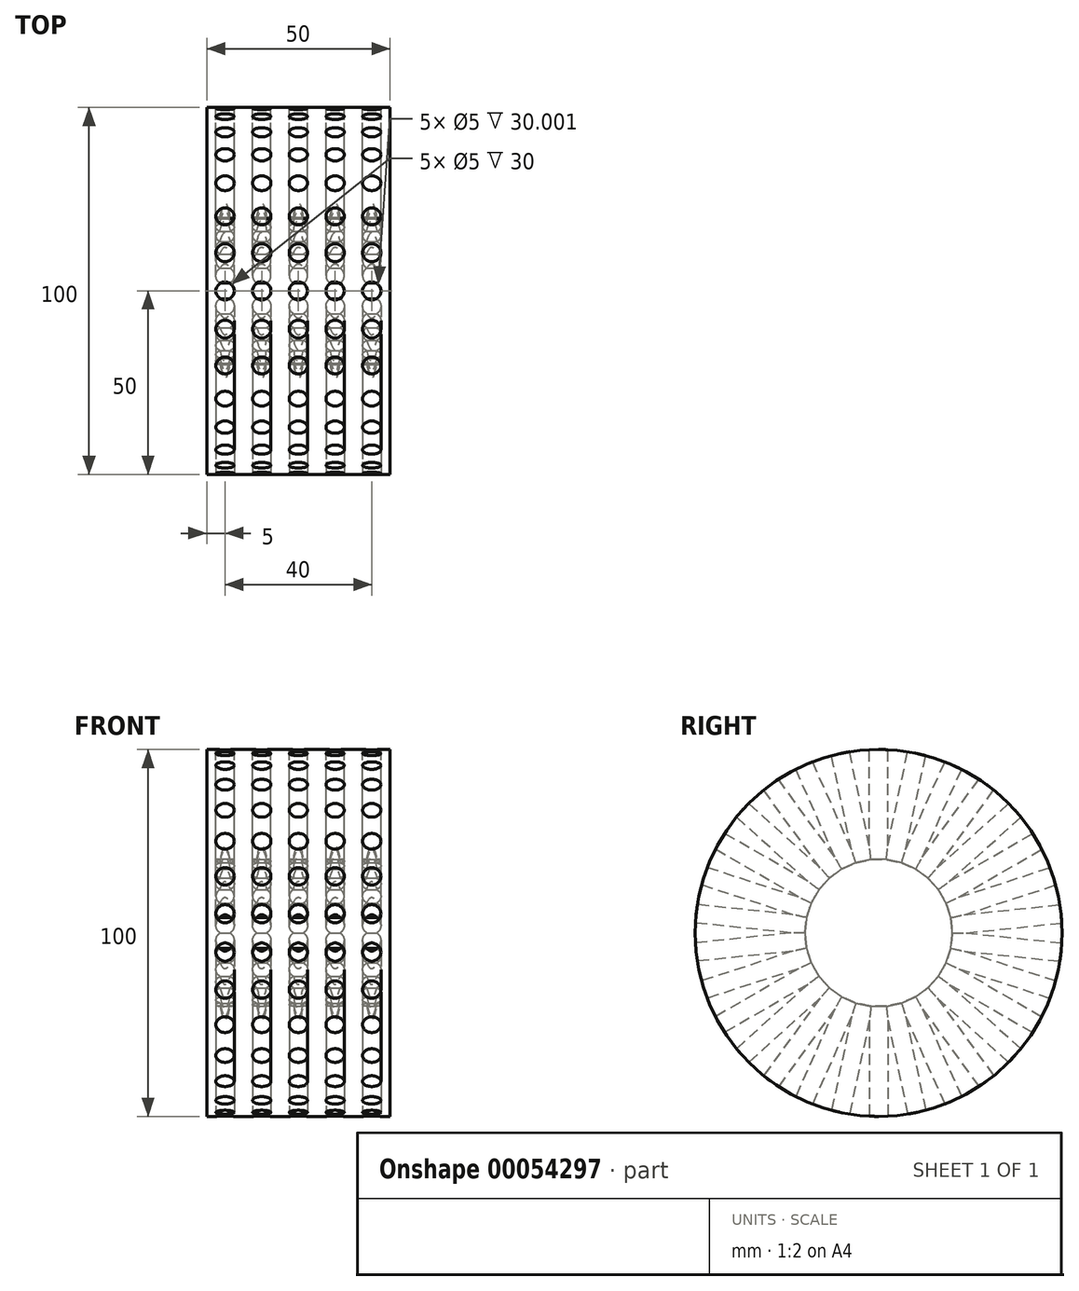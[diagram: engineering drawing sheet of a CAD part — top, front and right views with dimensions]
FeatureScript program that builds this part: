
annotation { "Feature Type Name" : "Feature", "Feature Type Description" : "" }
export const myFeature = defineFeature(function(context is Context, id is Id, definition is map)
    precondition{}
    {
        {
            var Q0;
            Q0=qCreatedBy(makeId("Right.planeOp"),FACE);
            var sketch = newSketch(context, id + "F0", { "sketchPlane" : qUnion([Q0])});
            skCircle(sketch, "E0", {"center": v(0, 0) * mm, "radius": 50 * mm});
            skPoint(sketch, "E1", {"position": v(0, 50) * mm});
            skLineSegment(sketch, "E2", {"start": v(0, 50) * mm, "end": v(0, -50) * mm, "construction": true});
            skSolve(sketch);
        }
        {
            var Q0;
            Q0=makeQuery(id+"F0.imprint","IMPRINT",FACE,{"disambiguationData":[TD([[makeQuery(id+"F0.imprint","IMPRINT",EDGE,{"derivedFrom":sQuery(id+"F0.wireOp",EDGE,"E0")}),1.0]])]});
            extrude(context, id + "F1", {"entities" : qUnion([Q0]), "depth" : 50 * mm});
        }
        {
            var Q0;
            Q0=sQuery(id+"F0.wireOp",VERTEX,"E1");
            var Q1;
            Q1=sQuery(id+"F0.wireOp",EDGE,"E2");
            cPlane(context, id + "F2", {"entities" : qUnion([Q0, Q1]), "cplaneType" : CPlaneType.LINE_POINT, "offset" : 150 * mm, "width" : 150 * mm, "height" : 150 * mm});
        }
        {
            var Q0;
            Q0=qCreatedBy(id+"F2.planeOp",FACE);
            var sketch = newSketch(context, id + "F3", { "sketchPlane" : qUnion([Q0])});
            skLineSegment(sketch, "E3", {"start": v(0, 0) * mm, "end": v(50, 0) * mm, "construction": true});
            skLineSegment(sketch, "E4.0", {"start": v(50, 50) * mm, "end": v(50, -50) * mm, "construction": true});
            skCircle(sketch, "E5", {"center": v(5, 0) * mm, "radius": 2.5 * mm});
            skCircle(sketch, "E6.1.0.0", {"center": v(15, 0) * mm, "radius": 2.5 * mm});
            skCircle(sketch, "E6.2.0.0", {"center": v(25, 0) * mm, "radius": 2.5 * mm});
            skCircle(sketch, "E6.3.0.0", {"center": v(35, 0) * mm, "radius": 2.5 * mm});
            skCircle(sketch, "E6.4.0.0", {"center": v(45, 0) * mm, "radius": 2.5 * mm});
            skLineSegment(sketch, "E6.direction1", {"start": v(5, 0) * mm, "end": v(15, 0) * mm, "construction": true});
            skSolve(sketch);
        }
        {
            var Q0;
            Q0 = qSketchRegion(id + "F3", true);
            extrude(context, id + "F4", {"entities" : qUnion([Q0]), "depth" : 30 * mm});
        }
        {
            var Q0;
            Q0=qCreatedBy(makeId("Front.planeOp"),FACE);
            var sketch = newSketch(context, id + "F5", { "sketchPlane" : qUnion([Q0])});
            skLineSegment(sketch, "E7", {"start": v(0, 0) * mm, "end": v(40.86, 0) * mm, "construction": true});
            skSolve(sketch);
        }
        {
            var Q0;
            Q0=makeQuery(id+"F4.opExtrude","SWEPT_BODY",BODY,{"disambiguationData":[OSD([sQuery(id+"F3.wireOp",EDGE,"E5")])]});
            var Q1;
            Q1=makeQuery(id+"F4.opExtrude","SWEPT_BODY",BODY,{"disambiguationData":[OSD([sQuery(id+"F3.wireOp",EDGE,"E6.1.0.0")])]});
            var Q2;
            Q2=makeQuery(id+"F4.opExtrude","SWEPT_BODY",BODY,{"disambiguationData":[OSD([sQuery(id+"F3.wireOp",EDGE,"E6.2.0.0")])]});
            var Q3;
            Q3=makeQuery(id+"F4.opExtrude","SWEPT_BODY",BODY,{"disambiguationData":[OSD([sQuery(id+"F3.wireOp",EDGE,"E6.3.0.0")])]});
            var Q4;
            Q4=makeQuery(id+"F4.opExtrude","SWEPT_BODY",BODY,{"disambiguationData":[OSD([sQuery(id+"F3.wireOp",EDGE,"E6.4.0.0")])]});
            var Q5;
            Q5=sQuery(id+"F5.wireOp",EDGE,"E7");
            var Q6;
            Q6=makeQuery(id+"F1.opExtrude","SWEPT_BODY",BODY,{"disambiguationData":[OSD([sQuery(id+"F0.wireOp",EDGE,"E0")])]});
            circularPattern(context, id + "F6", {"operationType" : NewBodyOperationType.REMOVE, "entities" : qUnion([Q0, Q1, Q2, Q3, Q4]), "axis" : qUnion([Q5]), "angle" : 360 * degree, "instanceCount" : 30, "equalSpace" : true});
        }
    });
